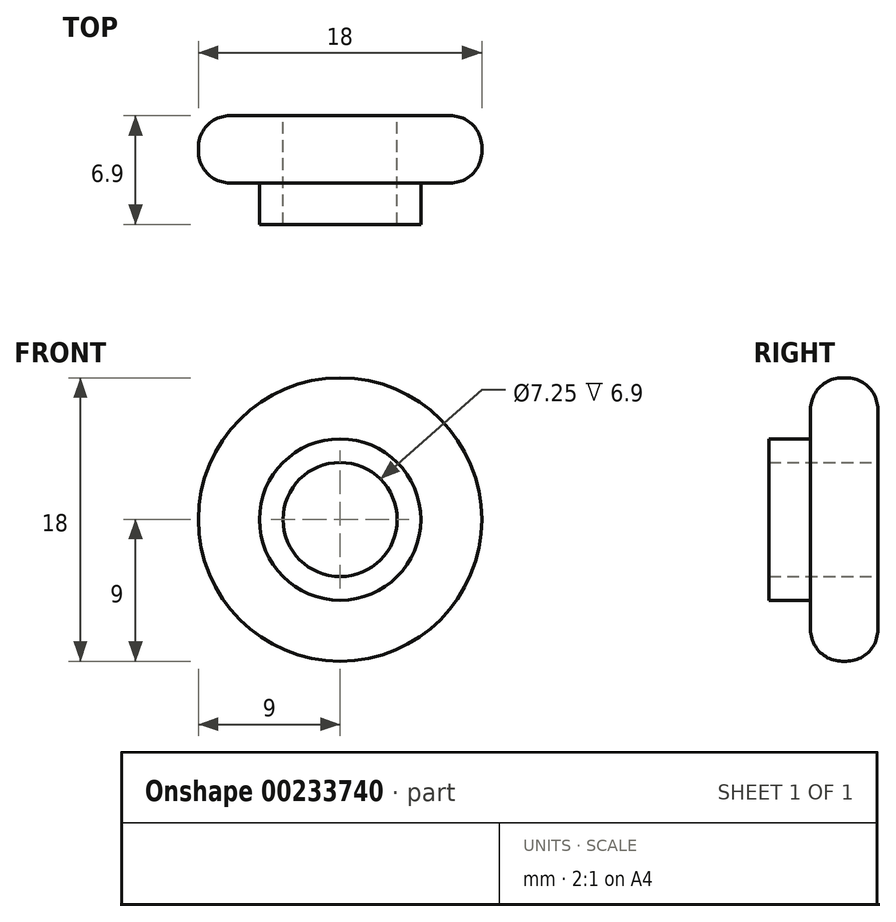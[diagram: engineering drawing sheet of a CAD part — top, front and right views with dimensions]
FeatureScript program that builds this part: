
annotation { "Feature Type Name" : "Feature", "Feature Type Description" : "" }
export const myFeature = defineFeature(function(context is Context, id is Id, definition is map)
    precondition{}
    {
        {
            var Q0;
            Q0=qCreatedBy(makeId("Front.planeOp"),FACE);
            var sketch = newSketch(context, id + "F0", { "sketchPlane" : qUnion([Q0])});
            skCircle(sketch, "E0", {"center": v(0, 0) * mm, "radius": 9 * mm});
            skCircle(sketch, "E1", {"center": v(0, 0) * mm, "radius": 5.12 * mm});
            skCircle(sketch, "E2", {"center": v(0, 0) * mm, "radius": 3.62 * mm});
            skSolve(sketch);
        }
        {
            var Q0;
            Q0=makeQuery(id+"F0.imprint","IMPRINT",FACE,{"disambiguationData":[TD([[makeQuery(id+"F0.imprint","IMPRINT",EDGE,{"derivedFrom":sQuery(id+"F0.wireOp",EDGE,"E0")}),1.0]])]});
            extrude(context, id + "F1", {"entities" : qUnion([Q0]), "depth" : 4.27 * mm});
        }
        {
            var Q0;
            Q0=makeQuery(id+"F0.imprint","IMPRINT",FACE,{"disambiguationData":[TD([[makeQuery(id+"F0.imprint","IMPRINT",EDGE,{"derivedFrom":sQuery(id+"F0.wireOp",EDGE,"E1")}),1.0]])]});
            extrude(context, id + "F2", {"entities" : qUnion([Q0]), "operationType" : NewBodyOperationType.ADD, "depth" : 6.9 * mm});
        }
        {
            var Q0;
            Q0=makeQuery(id+"F1.opExtrude","CAP_EDGE",EDGE,{"disambiguationData":[OSD([sQuery(id+"F0.wireOp",EDGE,"E0")])],"isStart":false});
            var Q1;
            Q1=makeQuery(id+"F1.opExtrude","CAP_EDGE",EDGE,{"disambiguationData":[OSD([sQuery(id+"F0.wireOp",EDGE,"E0")])],"isStart":true});
            fillet(context, id + "F3", {"entities" : qUnion([Q0, Q1]), "radius" : 2 * mm, "tangentPropagation" : true, "allowEdgeOverflow" : false});
        }
    });
